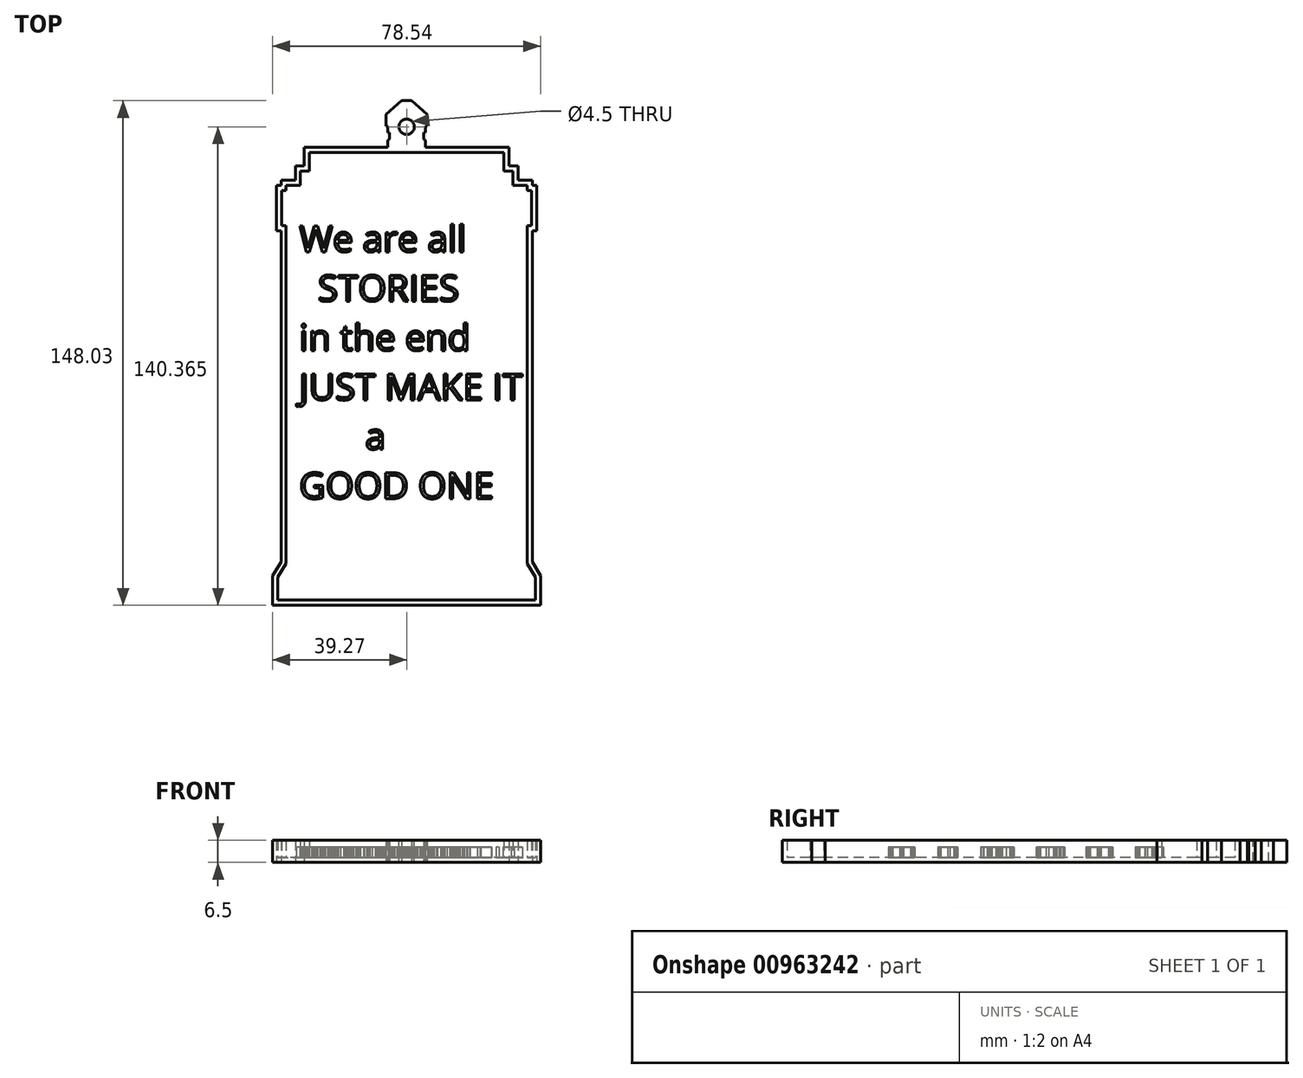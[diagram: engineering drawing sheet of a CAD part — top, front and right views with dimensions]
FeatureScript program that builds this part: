
annotation { "Feature Type Name" : "Feature", "Feature Type Description" : "" }
export const myFeature = defineFeature(function(context is Context, id is Id, definition is map)
    precondition{}
    {
        {
            var Q0;
            Q0=qCreatedBy(makeId("Top.planeOp"),FACE);
            var sketch = newSketch(context, id + "F0", { "sketchPlane" : qUnion([Q0])});
            skLineSegment(sketch, "E0", {"start": v(0, 73.78) * mm, "end": v(0.9, 73.78) * mm});
            skLineSegment(sketch, "E1", {"start": v(0.9, 73.78) * mm, "end": v(4.5, 70.6) * mm});
            skLineSegment(sketch, "E2", {"start": v(4.5, 70.6) * mm, "end": v(4.5, 69.3) * mm});
            skLineSegment(sketch, "E3", {"start": v(4.5, 69.3) * mm, "end": v(3.98, 69.3) * mm});
            skLineSegment(sketch, "E4", {"start": v(3.98, 69.3) * mm, "end": v(3.98, 67.46) * mm});
            skLineSegment(sketch, "E5", {"start": v(3.98, 67.46) * mm, "end": v(3.5, 67.46) * mm});
            skLineSegment(sketch, "E6", {"start": v(3.5, 67.46) * mm, "end": v(3.5, 63.47) * mm});
            skLineSegment(sketch, "E7", {"start": v(3.5, 63.47) * mm, "end": v(3.7, 63.14) * mm});
            skLineSegment(sketch, "E8", {"start": v(3.7, 63.14) * mm, "end": v(4.06, 62.9) * mm});
            skLineSegment(sketch, "E9", {"start": v(4.06, 62.9) * mm, "end": v(4.06, 60.05) * mm});
            skLineSegment(sketch, "E10", {"start": v(4.06, 60.05) * mm, "end": v(28.54, 60.05) * mm});
            skLineSegment(sketch, "E11", {"start": v(28.54, 60.05) * mm, "end": v(28.54, 54.6) * mm});
            skLineSegment(sketch, "E12", {"start": v(28.54, 54.6) * mm, "end": v(31.15, 54.6) * mm});
            skLineSegment(sketch, "E13", {"start": v(31.15, 54.6) * mm, "end": v(31.15, 50.48) * mm});
            skLineSegment(sketch, "E14", {"start": v(31.15, 50.48) * mm, "end": v(35.32, 50.48) * mm});
            skLineSegment(sketch, "E15", {"start": v(35.32, 50.48) * mm, "end": v(35.32, 48.89) * mm});
            skLineSegment(sketch, "E16", {"start": v(35.32, 48.89) * mm, "end": v(36.65, 48.89) * mm});
            skLineSegment(sketch, "E17", {"start": v(36.65, 48.89) * mm, "end": v(36.65, 38.6) * mm});
            skLineSegment(sketch, "E18", {"start": v(36.65, 38.6) * mm, "end": v(35.32, 38.6) * mm});
            skLineSegment(sketch, "E19", {"start": v(35.32, 38.6) * mm, "end": v(35.32, -60.55) * mm});
            skLineSegment(sketch, "E20", {"start": v(35.32, -60.55) * mm, "end": v(37.77, -64.54) * mm});
            skLineSegment(sketch, "E21", {"start": v(37.77, -64.54) * mm, "end": v(37.77, -71.25) * mm});
            skLineSegment(sketch, "E22", {"start": v(37.77, -71.25) * mm, "end": v(0, -71.25) * mm});
            skLineSegment(sketch, "E23.MirrorCS", {"start": v(-3.98, 69.3) * mm, "end": v(-3.98, 67.46) * mm});
            skLineSegment(sketch, "E24.MirrorCS", {"start": v(-4.5, 69.3) * mm, "end": v(-3.98, 69.3) * mm});
            skLineSegment(sketch, "E25.MirrorCS", {"start": v(-4.5, 70.6) * mm, "end": v(-4.5, 69.3) * mm});
            skLineSegment(sketch, "E26.MirrorCS", {"start": v(-3.98, 67.46) * mm, "end": v(-3.5, 67.46) * mm});
            skLineSegment(sketch, "E27.MirrorCS", {"start": v(-3.5, 63.47) * mm, "end": v(-3.7, 63.14) * mm});
            skLineSegment(sketch, "E28.MirrorCS", {"start": v(-0.9, 73.78) * mm, "end": v(-4.5, 70.6) * mm});
            skLineSegment(sketch, "E29.MirrorCS", {"start": v(0, 73.78) * mm, "end": v(-0.9, 73.78) * mm});
            skLineSegment(sketch, "E30.MirrorCS", {"start": v(-35.32, 50.48) * mm, "end": v(-35.32, 48.89) * mm});
            skLineSegment(sketch, "E31.MirrorCS", {"start": v(-3.7, 63.14) * mm, "end": v(-4.06, 62.9) * mm});
            skLineSegment(sketch, "E32.MirrorCS", {"start": v(-28.54, 60.05) * mm, "end": v(-28.54, 54.6) * mm});
            skLineSegment(sketch, "E33.MirrorCS", {"start": v(-35.32, 48.89) * mm, "end": v(-36.65, 48.89) * mm});
            skLineSegment(sketch, "E34.MirrorCS", {"start": v(-36.65, 38.6) * mm, "end": v(-35.32, 38.6) * mm});
            skLineSegment(sketch, "E35.MirrorCS", {"start": v(-37.77, -64.54) * mm, "end": v(-37.77, -71.25) * mm});
            skLineSegment(sketch, "E36.MirrorCS", {"start": v(-28.54, 54.6) * mm, "end": v(-31.15, 54.6) * mm});
            skLineSegment(sketch, "E37.MirrorCS", {"start": v(-31.15, 50.48) * mm, "end": v(-35.32, 50.48) * mm});
            skLineSegment(sketch, "E38.MirrorCS", {"start": v(-4.06, 62.9) * mm, "end": v(-4.06, 60.05) * mm});
            skLineSegment(sketch, "E39.MirrorCS", {"start": v(-3.5, 67.46) * mm, "end": v(-3.5, 63.47) * mm});
            skLineSegment(sketch, "E40.MirrorCS", {"start": v(-31.15, 54.6) * mm, "end": v(-31.15, 50.48) * mm});
            skLineSegment(sketch, "E41.MirrorCS", {"start": v(-35.32, -60.55) * mm, "end": v(-37.77, -64.54) * mm});
            skLineSegment(sketch, "E42.MirrorCS", {"start": v(-37.77, -71.25) * mm, "end": v(0, -71.25) * mm});
            skLineSegment(sketch, "E43.MirrorCS", {"start": v(-35.32, 38.6) * mm, "end": v(-35.32, -60.55) * mm});
            skLineSegment(sketch, "E44.MirrorCS", {"start": v(-4.06, 60.05) * mm, "end": v(-28.54, 60.05) * mm});
            skLineSegment(sketch, "E45.MirrorCS", {"start": v(-36.65, 48.89) * mm, "end": v(-36.65, 38.6) * mm});
            skSolve(sketch);
        }
        {
            var Q0;
            Q0=makeQuery(id+"F0.imprint","IMPRINT",FACE,{"disambiguationData":[TD([[makeQuery(id+"F0.imprint","IMPRINT",EDGE,{"derivedFrom":sQuery(id+"F0.wireOp",EDGE,"E0")}),-1.0]])]});
            extrude(context, id + "F1", {"entities" : qUnion([Q0]), "depth" : 5 * mm, "offsetDistance" : 25 * mm});
        }
        {
            var Q0;
            Q0=makeQuery(id+"F1.opExtrude","CAP_FACE",FACE,{"disambiguationData":[OSD([sQuery(id+"F0.wireOp",EDGE,"E0"),sQuery(id+"F0.wireOp",EDGE,"E1"),sQuery(id+"F0.wireOp",EDGE,"E2"),sQuery(id+"F0.wireOp",EDGE,"E3"),sQuery(id+"F0.wireOp",EDGE,"E4"),sQuery(id+"F0.wireOp",EDGE,"E5"),sQuery(id+"F0.wireOp",EDGE,"E6"),sQuery(id+"F0.wireOp",EDGE,"E7"),sQuery(id+"F0.wireOp",EDGE,"E8"),sQuery(id+"F0.wireOp",EDGE,"E9"),sQuery(id+"F0.wireOp",EDGE,"E10"),sQuery(id+"F0.wireOp",EDGE,"E11"),sQuery(id+"F0.wireOp",EDGE,"E12"),sQuery(id+"F0.wireOp",EDGE,"E13"),sQuery(id+"F0.wireOp",EDGE,"E14"),sQuery(id+"F0.wireOp",EDGE,"E15"),sQuery(id+"F0.wireOp",EDGE,"E16"),sQuery(id+"F0.wireOp",EDGE,"E17"),sQuery(id+"F0.wireOp",EDGE,"E18"),sQuery(id+"F0.wireOp",EDGE,"E19"),sQuery(id+"F0.wireOp",EDGE,"E20"),sQuery(id+"F0.wireOp",EDGE,"E21"),sQuery(id+"F0.wireOp",EDGE,"E22"),sQuery(id+"F0.wireOp",EDGE,"E23.MirrorCS"),sQuery(id+"F0.wireOp",EDGE,"E24.MirrorCS"),sQuery(id+"F0.wireOp",EDGE,"E25.MirrorCS"),sQuery(id+"F0.wireOp",EDGE,"E26.MirrorCS"),sQuery(id+"F0.wireOp",EDGE,"E27.MirrorCS"),sQuery(id+"F0.wireOp",EDGE,"E28.MirrorCS"),sQuery(id+"F0.wireOp",EDGE,"E29.MirrorCS"),sQuery(id+"F0.wireOp",EDGE,"E30.MirrorCS"),sQuery(id+"F0.wireOp",EDGE,"E31.MirrorCS"),sQuery(id+"F0.wireOp",EDGE,"E32.MirrorCS"),sQuery(id+"F0.wireOp",EDGE,"E33.MirrorCS"),sQuery(id+"F0.wireOp",EDGE,"E34.MirrorCS"),sQuery(id+"F0.wireOp",EDGE,"E35.MirrorCS"),sQuery(id+"F0.wireOp",EDGE,"E36.MirrorCS"),sQuery(id+"F0.wireOp",EDGE,"E37.MirrorCS"),sQuery(id+"F0.wireOp",EDGE,"E38.MirrorCS"),sQuery(id+"F0.wireOp",EDGE,"E39.MirrorCS"),sQuery(id+"F0.wireOp",EDGE,"E40.MirrorCS"),sQuery(id+"F0.wireOp",EDGE,"E41.MirrorCS"),sQuery(id+"F0.wireOp",EDGE,"E42.MirrorCS"),sQuery(id+"F0.wireOp",EDGE,"E43.MirrorCS"),sQuery(id+"F0.wireOp",EDGE,"E44.MirrorCS"),sQuery(id+"F0.wireOp",EDGE,"E45.MirrorCS")])],"isStart":false});
            shell(context, id + "F2", {"entities" : qUnion([Q0]), "thickness" : 1.5 * mm, "oppositeDirection" : true});
        }
        {
            var Q0;
            Q0=makeQuery(id+"F2.opShell","OFFSET_FACE",FACE,{"disambiguationData":[OSD([sQuery(id+"F0.wireOp",EDGE,"E0"),sQuery(id+"F0.wireOp",EDGE,"E1"),sQuery(id+"F0.wireOp",EDGE,"E2"),sQuery(id+"F0.wireOp",EDGE,"E3"),sQuery(id+"F0.wireOp",EDGE,"E4"),sQuery(id+"F0.wireOp",EDGE,"E5"),sQuery(id+"F0.wireOp",EDGE,"E6"),sQuery(id+"F0.wireOp",EDGE,"E7"),sQuery(id+"F0.wireOp",EDGE,"E8"),sQuery(id+"F0.wireOp",EDGE,"E9"),sQuery(id+"F0.wireOp",EDGE,"E10"),sQuery(id+"F0.wireOp",EDGE,"E11"),sQuery(id+"F0.wireOp",EDGE,"E12"),sQuery(id+"F0.wireOp",EDGE,"E13"),sQuery(id+"F0.wireOp",EDGE,"E14"),sQuery(id+"F0.wireOp",EDGE,"E15"),sQuery(id+"F0.wireOp",EDGE,"E16"),sQuery(id+"F0.wireOp",EDGE,"E17"),sQuery(id+"F0.wireOp",EDGE,"E18"),sQuery(id+"F0.wireOp",EDGE,"E19"),sQuery(id+"F0.wireOp",EDGE,"E20"),sQuery(id+"F0.wireOp",EDGE,"E21"),sQuery(id+"F0.wireOp",EDGE,"E22"),sQuery(id+"F0.wireOp",EDGE,"E23.MirrorCS"),sQuery(id+"F0.wireOp",EDGE,"E24.MirrorCS"),sQuery(id+"F0.wireOp",EDGE,"E25.MirrorCS"),sQuery(id+"F0.wireOp",EDGE,"E26.MirrorCS"),sQuery(id+"F0.wireOp",EDGE,"E27.MirrorCS"),sQuery(id+"F0.wireOp",EDGE,"E28.MirrorCS"),sQuery(id+"F0.wireOp",EDGE,"E29.MirrorCS"),sQuery(id+"F0.wireOp",EDGE,"E30.MirrorCS"),sQuery(id+"F0.wireOp",EDGE,"E31.MirrorCS"),sQuery(id+"F0.wireOp",EDGE,"E32.MirrorCS"),sQuery(id+"F0.wireOp",EDGE,"E33.MirrorCS"),sQuery(id+"F0.wireOp",EDGE,"E34.MirrorCS"),sQuery(id+"F0.wireOp",EDGE,"E35.MirrorCS"),sQuery(id+"F0.wireOp",EDGE,"E36.MirrorCS"),sQuery(id+"F0.wireOp",EDGE,"E37.MirrorCS"),sQuery(id+"F0.wireOp",EDGE,"E38.MirrorCS"),sQuery(id+"F0.wireOp",EDGE,"E39.MirrorCS"),sQuery(id+"F0.wireOp",EDGE,"E40.MirrorCS"),sQuery(id+"F0.wireOp",EDGE,"E41.MirrorCS"),sQuery(id+"F0.wireOp",EDGE,"E42.MirrorCS"),sQuery(id+"F0.wireOp",EDGE,"E43.MirrorCS"),sQuery(id+"F0.wireOp",EDGE,"E44.MirrorCS"),sQuery(id+"F0.wireOp",EDGE,"E45.MirrorCS")])]});
            var sketch = newSketch(context, id + "F3", { "sketchPlane" : qUnion([Q0])});
            skText(sketch, "E46", { "text": "We are all\n  STORIES\nin the end\nJUST MAKE IT\n       a\nGOOD ONE", "fontName": "OpenSans-Regular.ttf"});
            skPoint(sketch, "E47", {"position": v(0, 69.3) * mm});
            const initialGuessF3  = {"E46": [-0.03152, 0.03093, 1, 0, 0.00767]};
            skSetInitialGuess(sketch, initialGuessF3);
            skSolve(sketch);
        }
        {
            var Q0;
            Q0 = qSketchRegion(id + "F3", true);
            extrude(context, id + "F4", {"entities" : qUnion([Q0]), "operationType" : NewBodyOperationType.ADD, "depth" : 3 * mm, "offsetDistance" : 25 * mm});
        }
        {
            var Q0;
            {var subQ0=sQuery(id+"F0.wireOp",EDGE,"E31.MirrorCS");var subQ1=sQuery(id+"F0.wireOp",EDGE,"E30.MirrorCS");var subQ2=sQuery(id+"F0.wireOp",EDGE,"E28.MirrorCS");var subQ3=sQuery(id+"F0.wireOp",EDGE,"E27.MirrorCS");var subQ4=sQuery(id+"F0.wireOp",EDGE,"E26.MirrorCS");var subQ5=sQuery(id+"F0.wireOp",EDGE,"E25.MirrorCS");var subQ6=sQuery(id+"F0.wireOp",EDGE,"E24.MirrorCS");var subQ7=sQuery(id+"F0.wireOp",EDGE,"E23.MirrorCS");var subQ8=sQuery(id+"F0.wireOp",EDGE,"E42.MirrorCS");var subQ9=sQuery(id+"F0.wireOp",EDGE,"E22");var subQ10=sQuery(id+"F0.wireOp",EDGE,"E21");var subQ11=sQuery(id+"F0.wireOp",EDGE,"E20");var subQ12=sQuery(id+"F0.wireOp",EDGE,"E17");var subQ13=sQuery(id+"F0.wireOp",EDGE,"E16");var subQ14=sQuery(id+"F0.wireOp",EDGE,"E15");var subQ15=sQuery(id+"F0.wireOp",EDGE,"E14");var subQ16=sQuery(id+"F0.wireOp",EDGE,"E13");var subQ17=sQuery(id+"F0.wireOp",EDGE,"E12");var subQ18=sQuery(id+"F0.wireOp",EDGE,"E11");var subQ19=sQuery(id+"F0.wireOp",EDGE,"E10");var subQ20=sQuery(id+"F0.wireOp",EDGE,"E9");var subQ21=sQuery(id+"F0.wireOp",EDGE,"E8");var subQ22=sQuery(id+"F0.wireOp",EDGE,"E7");var subQ23=sQuery(id+"F0.wireOp",EDGE,"E6");var subQ24=sQuery(id+"F0.wireOp",EDGE,"E5");var subQ25=sQuery(id+"F0.wireOp",EDGE,"E4");var subQ26=sQuery(id+"F0.wireOp",EDGE,"E3");var subQ27=sQuery(id+"F0.wireOp",EDGE,"E2");var subQ28=sQuery(id+"F0.wireOp",EDGE,"E1");var subQ29=sQuery(id+"F0.wireOp",EDGE,"E29.MirrorCS");var subQ30=sQuery(id+"F0.wireOp",EDGE,"E0");var subQ31=sQuery(id+"F0.wireOp",EDGE,"E19");var subQ32=sQuery(id+"F0.wireOp",EDGE,"E18");var subQ33=sQuery(id+"F0.wireOp",EDGE,"E45.MirrorCS");var subQ34=sQuery(id+"F0.wireOp",EDGE,"E44.MirrorCS");var subQ35=sQuery(id+"F0.wireOp",EDGE,"E43.MirrorCS");var subQ36=sQuery(id+"F0.wireOp",EDGE,"E33.MirrorCS");var subQ37=sQuery(id+"F0.wireOp",EDGE,"E32.MirrorCS");var subQ38=sQuery(id+"F0.wireOp",EDGE,"E39.MirrorCS");var subQ39=sQuery(id+"F0.wireOp",EDGE,"E34.MirrorCS");var subQ40=sQuery(id+"F0.wireOp",EDGE,"E35.MirrorCS");var subQ41=sQuery(id+"F0.wireOp",EDGE,"E36.MirrorCS");var subQ42=sQuery(id+"F0.wireOp",EDGE,"E37.MirrorCS");var subQ43=sQuery(id+"F0.wireOp",EDGE,"E38.MirrorCS");var subQ44=sQuery(id+"F0.wireOp",EDGE,"E40.MirrorCS");var subQ45=sQuery(id+"F0.wireOp",EDGE,"E41.MirrorCS");Q0=makeQuery(id+"F4.boolean.opBoolean","SPLIT",FACE,{"disambiguationData":[TD([makeQuery(id+"F2.opShell","OFFSET_FACE",FACE,{"disambiguationData":[OSD([subQ28])]})])],"derivedFrom":makeQuery(id+"F2.opShell","OFFSET_FACE",FACE,{"disambiguationData":[OSD([subQ30,subQ28,subQ27,subQ26,subQ25,subQ24,subQ23,subQ22,subQ21,subQ20,subQ19,subQ18,subQ17,subQ16,subQ15,subQ14,subQ13,subQ12,subQ32,subQ31,subQ11,subQ10,subQ9,subQ7,subQ6,subQ5,subQ4,subQ3,subQ2,subQ29,subQ1,subQ0,subQ37,subQ36,subQ39,subQ40,subQ41,subQ42,subQ43,subQ38,subQ44,subQ45,subQ8,subQ35,subQ34,subQ33])]})});}
            var sketch = newSketch(context, id + "F5", { "sketchPlane" : qUnion([Q0])});
            skLineSegment(sketch, "E48", {"start": v(0, 73.78) * mm, "end": v(0.9, 73.78) * mm});
            skLineSegment(sketch, "E49", {"start": v(0.9, 73.78) * mm, "end": v(4.5, 70.6) * mm});
            skLineSegment(sketch, "E50", {"start": v(4.5, 70.6) * mm, "end": v(4.5, 69.3) * mm});
            skLineSegment(sketch, "E51", {"start": v(4.5, 69.3) * mm, "end": v(3.98, 69.3) * mm});
            skLineSegment(sketch, "E52", {"start": v(3.98, 69.3) * mm, "end": v(3.98, 67.46) * mm});
            skLineSegment(sketch, "E53", {"start": v(3.98, 67.46) * mm, "end": v(3.5, 67.46) * mm});
            skLineSegment(sketch, "E54", {"start": v(3.5, 67.46) * mm, "end": v(3.5, 63.47) * mm});
            skLineSegment(sketch, "E55", {"start": v(3.5, 63.47) * mm, "end": v(3.7, 63.14) * mm});
            skLineSegment(sketch, "E56", {"start": v(3.7, 63.14) * mm, "end": v(4.06, 62.9) * mm});
            skLineSegment(sketch, "E57", {"start": v(4.06, 62.9) * mm, "end": v(4.06, 60.05) * mm});
            skLineSegment(sketch, "E58.MirrorCS", {"start": v(-3.98, 69.3) * mm, "end": v(-3.98, 67.46) * mm});
            skLineSegment(sketch, "E59.MirrorCS", {"start": v(-4.5, 69.3) * mm, "end": v(-3.98, 69.3) * mm});
            skLineSegment(sketch, "E60.MirrorCS", {"start": v(-4.5, 70.6) * mm, "end": v(-4.5, 69.3) * mm});
            skLineSegment(sketch, "E61.MirrorCS", {"start": v(-3.98, 67.46) * mm, "end": v(-3.5, 67.46) * mm});
            skLineSegment(sketch, "E62.MirrorCS", {"start": v(-3.5, 63.47) * mm, "end": v(-3.7, 63.14) * mm});
            skLineSegment(sketch, "E63.MirrorCS", {"start": v(-0.9, 73.78) * mm, "end": v(-4.5, 70.6) * mm});
            skLineSegment(sketch, "E64.MirrorCS", {"start": v(0, 73.78) * mm, "end": v(-0.9, 73.78) * mm});
            skLineSegment(sketch, "E65.MirrorCS", {"start": v(-3.7, 63.14) * mm, "end": v(-4.06, 62.9) * mm});
            skLineSegment(sketch, "E66.MirrorCS", {"start": v(-4.06, 62.9) * mm, "end": v(-4.06, 60.05) * mm});
            skLineSegment(sketch, "E67.MirrorCS", {"start": v(-3.5, 67.46) * mm, "end": v(-3.5, 63.47) * mm});
            skLineSegment(sketch, "E68", {"start": v(-4.06, 60.05) * mm, "end": v(4.06, 60.05) * mm});
            skSolve(sketch);
        }
        {
            var Q0;
            Q0 = qSketchRegion(id + "F5", true);
            extrude(context, id + "F6", {"entities" : qUnion([Q0]), "operationType" : NewBodyOperationType.ADD, "depth" : 5 * mm, "offsetDistance" : 25 * mm});
        }
        {
            var Q0;
            Q0=makeQuery(id+"F6.boolean.opBoolean","MERGE",FACE,{"derivedFrom":[makeQuery(id+"F1.opExtrude","CAP_FACE",FACE,{"disambiguationData":[OSD([sQuery(id+"F0.wireOp",EDGE,"E0"),sQuery(id+"F0.wireOp",EDGE,"E1"),sQuery(id+"F0.wireOp",EDGE,"E2"),sQuery(id+"F0.wireOp",EDGE,"E3"),sQuery(id+"F0.wireOp",EDGE,"E4"),sQuery(id+"F0.wireOp",EDGE,"E5"),sQuery(id+"F0.wireOp",EDGE,"E6"),sQuery(id+"F0.wireOp",EDGE,"E7"),sQuery(id+"F0.wireOp",EDGE,"E8"),sQuery(id+"F0.wireOp",EDGE,"E9"),sQuery(id+"F0.wireOp",EDGE,"E10"),sQuery(id+"F0.wireOp",EDGE,"E11"),sQuery(id+"F0.wireOp",EDGE,"E12"),sQuery(id+"F0.wireOp",EDGE,"E13"),sQuery(id+"F0.wireOp",EDGE,"E14"),sQuery(id+"F0.wireOp",EDGE,"E15"),sQuery(id+"F0.wireOp",EDGE,"E16"),sQuery(id+"F0.wireOp",EDGE,"E17"),sQuery(id+"F0.wireOp",EDGE,"E18"),sQuery(id+"F0.wireOp",EDGE,"E19"),sQuery(id+"F0.wireOp",EDGE,"E20"),sQuery(id+"F0.wireOp",EDGE,"E21"),sQuery(id+"F0.wireOp",EDGE,"E22"),sQuery(id+"F0.wireOp",EDGE,"E23.MirrorCS"),sQuery(id+"F0.wireOp",EDGE,"E24.MirrorCS"),sQuery(id+"F0.wireOp",EDGE,"E25.MirrorCS"),sQuery(id+"F0.wireOp",EDGE,"E26.MirrorCS"),sQuery(id+"F0.wireOp",EDGE,"E27.MirrorCS"),sQuery(id+"F0.wireOp",EDGE,"E28.MirrorCS"),sQuery(id+"F0.wireOp",EDGE,"E29.MirrorCS"),sQuery(id+"F0.wireOp",EDGE,"E30.MirrorCS"),sQuery(id+"F0.wireOp",EDGE,"E31.MirrorCS"),sQuery(id+"F0.wireOp",EDGE,"E32.MirrorCS"),sQuery(id+"F0.wireOp",EDGE,"E33.MirrorCS"),sQuery(id+"F0.wireOp",EDGE,"E34.MirrorCS"),sQuery(id+"F0.wireOp",EDGE,"E35.MirrorCS"),sQuery(id+"F0.wireOp",EDGE,"E36.MirrorCS"),sQuery(id+"F0.wireOp",EDGE,"E37.MirrorCS"),sQuery(id+"F0.wireOp",EDGE,"E38.MirrorCS"),sQuery(id+"F0.wireOp",EDGE,"E39.MirrorCS"),sQuery(id+"F0.wireOp",EDGE,"E40.MirrorCS"),sQuery(id+"F0.wireOp",EDGE,"E41.MirrorCS"),sQuery(id+"F0.wireOp",EDGE,"E42.MirrorCS"),sQuery(id+"F0.wireOp",EDGE,"E43.MirrorCS"),sQuery(id+"F0.wireOp",EDGE,"E44.MirrorCS"),sQuery(id+"F0.wireOp",EDGE,"E45.MirrorCS")])],"isStart":false}),makeQuery(id+"F6.opExtrude","CAP_FACE",FACE,{"disambiguationData":[OSD([sQuery(id+"F5.wireOp",EDGE,"E48"),sQuery(id+"F5.wireOp",EDGE,"E49"),sQuery(id+"F5.wireOp",EDGE,"E50"),sQuery(id+"F5.wireOp",EDGE,"E51"),sQuery(id+"F5.wireOp",EDGE,"E52"),sQuery(id+"F5.wireOp",EDGE,"E53"),sQuery(id+"F5.wireOp",EDGE,"E54"),sQuery(id+"F5.wireOp",EDGE,"E55"),sQuery(id+"F5.wireOp",EDGE,"E56"),sQuery(id+"F5.wireOp",EDGE,"E57"),sQuery(id+"F5.wireOp",EDGE,"E58.MirrorCS"),sQuery(id+"F5.wireOp",EDGE,"E59.MirrorCS"),sQuery(id+"F5.wireOp",EDGE,"E60.MirrorCS"),sQuery(id+"F5.wireOp",EDGE,"E61.MirrorCS"),sQuery(id+"F5.wireOp",EDGE,"E62.MirrorCS"),sQuery(id+"F5.wireOp",EDGE,"E63.MirrorCS"),sQuery(id+"F5.wireOp",EDGE,"E64.MirrorCS"),sQuery(id+"F5.wireOp",EDGE,"E65.MirrorCS"),sQuery(id+"F5.wireOp",EDGE,"E66.MirrorCS"),sQuery(id+"F5.wireOp",EDGE,"E67.MirrorCS"),sQuery(id+"F5.wireOp",EDGE,"E68")])],"isStart":false})]});
            var sketch = newSketch(context, id + "F7", { "sketchPlane" : qUnion([Q0])});
            skPoint(sketch, "E69", {"position": v(0, 67.61) * mm});
            skSolve(sketch);
        }
        {
            var Q0;
            Q0=sQuery(id+"F7.wireOp",VERTEX,"E69");
            var Q1;
            Q1=makeQuery(id+"F1.opExtrude","SWEPT_BODY",BODY,{"disambiguationData":[OSD([sQuery(id+"F0.wireOp",EDGE,"E0"),sQuery(id+"F0.wireOp",EDGE,"E1"),sQuery(id+"F0.wireOp",EDGE,"E2"),sQuery(id+"F0.wireOp",EDGE,"E3"),sQuery(id+"F0.wireOp",EDGE,"E4"),sQuery(id+"F0.wireOp",EDGE,"E5"),sQuery(id+"F0.wireOp",EDGE,"E6"),sQuery(id+"F0.wireOp",EDGE,"E7"),sQuery(id+"F0.wireOp",EDGE,"E8"),sQuery(id+"F0.wireOp",EDGE,"E9"),sQuery(id+"F0.wireOp",EDGE,"E10"),sQuery(id+"F0.wireOp",EDGE,"E11"),sQuery(id+"F0.wireOp",EDGE,"E12"),sQuery(id+"F0.wireOp",EDGE,"E13"),sQuery(id+"F0.wireOp",EDGE,"E14"),sQuery(id+"F0.wireOp",EDGE,"E15"),sQuery(id+"F0.wireOp",EDGE,"E16"),sQuery(id+"F0.wireOp",EDGE,"E17"),sQuery(id+"F0.wireOp",EDGE,"E18"),sQuery(id+"F0.wireOp",EDGE,"E19"),sQuery(id+"F0.wireOp",EDGE,"E20"),sQuery(id+"F0.wireOp",EDGE,"E21"),sQuery(id+"F0.wireOp",EDGE,"E22"),sQuery(id+"F0.wireOp",EDGE,"E23.MirrorCS"),sQuery(id+"F0.wireOp",EDGE,"E24.MirrorCS"),sQuery(id+"F0.wireOp",EDGE,"E25.MirrorCS"),sQuery(id+"F0.wireOp",EDGE,"E26.MirrorCS"),sQuery(id+"F0.wireOp",EDGE,"E27.MirrorCS"),sQuery(id+"F0.wireOp",EDGE,"E28.MirrorCS"),sQuery(id+"F0.wireOp",EDGE,"E29.MirrorCS"),sQuery(id+"F0.wireOp",EDGE,"E30.MirrorCS"),sQuery(id+"F0.wireOp",EDGE,"E31.MirrorCS"),sQuery(id+"F0.wireOp",EDGE,"E32.MirrorCS"),sQuery(id+"F0.wireOp",EDGE,"E33.MirrorCS"),sQuery(id+"F0.wireOp",EDGE,"E34.MirrorCS"),sQuery(id+"F0.wireOp",EDGE,"E35.MirrorCS"),sQuery(id+"F0.wireOp",EDGE,"E36.MirrorCS"),sQuery(id+"F0.wireOp",EDGE,"E37.MirrorCS"),sQuery(id+"F0.wireOp",EDGE,"E38.MirrorCS"),sQuery(id+"F0.wireOp",EDGE,"E39.MirrorCS"),sQuery(id+"F0.wireOp",EDGE,"E40.MirrorCS"),sQuery(id+"F0.wireOp",EDGE,"E41.MirrorCS"),sQuery(id+"F0.wireOp",EDGE,"E42.MirrorCS"),sQuery(id+"F0.wireOp",EDGE,"E43.MirrorCS"),sQuery(id+"F0.wireOp",EDGE,"E44.MirrorCS"),sQuery(id+"F0.wireOp",EDGE,"E45.MirrorCS")])]});
            hole(context, id + "F8", {"style" : HoleStyle.SIMPLE, "endStyle" : HoleEndStyle.THROUGH, "standardTappedOrClearance" : lookupTablePath({ "fit" : "Normal", "standard" : "ISO", "size" : "M4", "type" : "Clearance" }), "standardBlindInLast" : lookupTablePath({ "fit" : "Normal", "standard" : "ISO", "engagement" : "75%", "pitch" : "0.7 mm", "size" : "M4", "type" : "Clearance & tapped" }), "holeDiameter" : 4.5 * mm, "majorDiameter" : 5 * mm, "isTappedThrough" : true, "tappedDepth" : 12 * mm, "tapClearance" : 3, "startFromSketch" : true, "locations" : qUnion([Q0]), "scope" : qUnion([Q1])});
        }
    });
